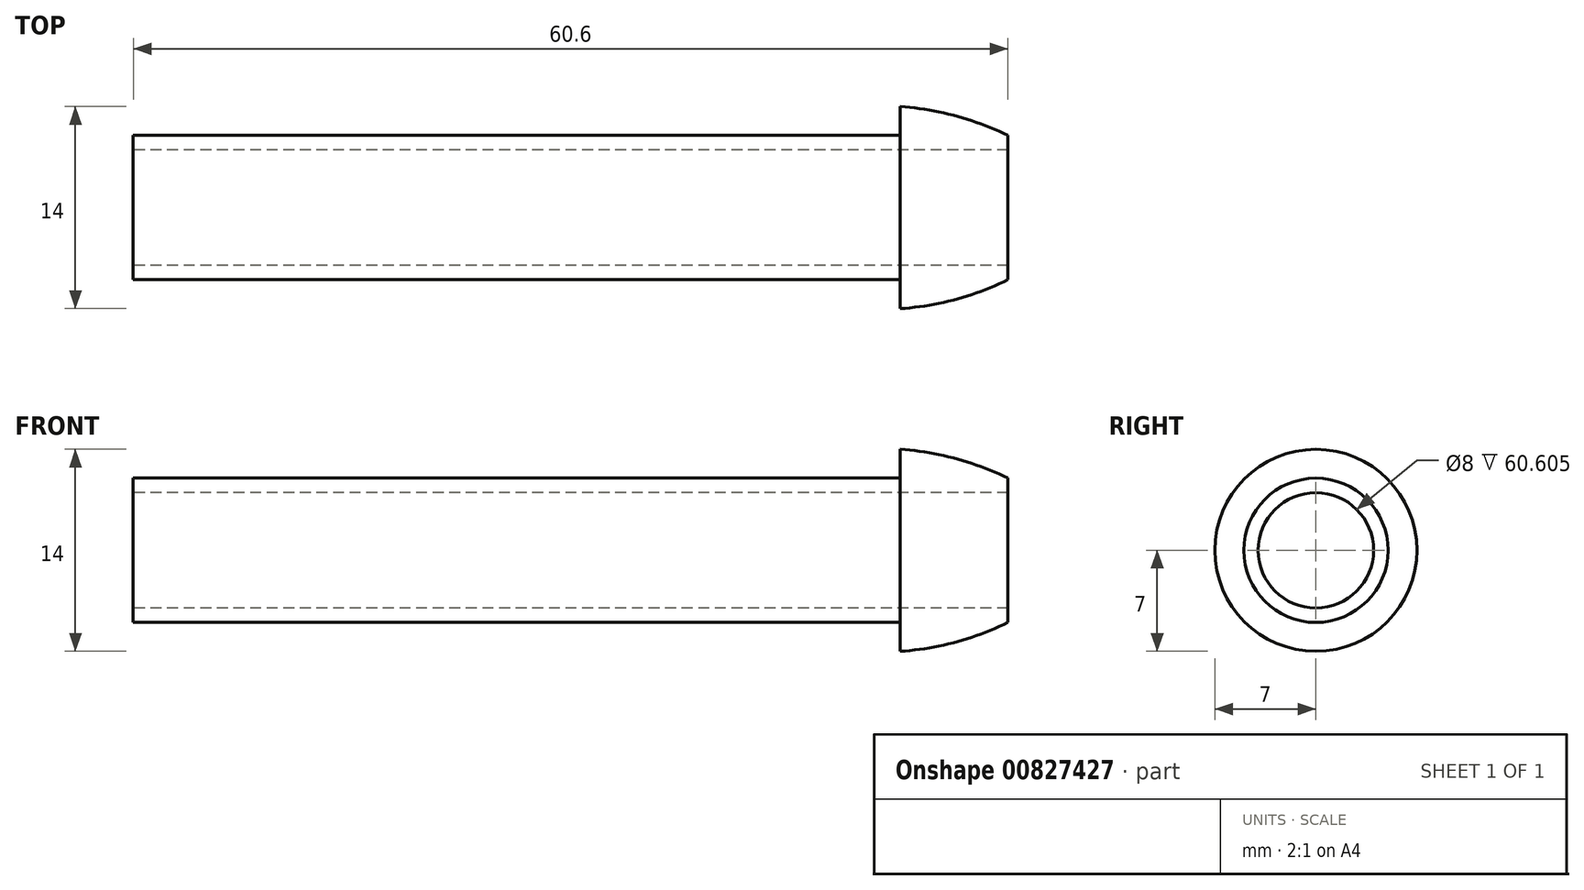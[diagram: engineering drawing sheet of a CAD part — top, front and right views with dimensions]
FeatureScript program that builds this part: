
annotation { "Feature Type Name" : "Feature", "Feature Type Description" : "" }
export const myFeature = defineFeature(function(context is Context, id is Id, definition is map)
    precondition{}
    {
        {
            var Q0;
            Q0=qCreatedBy(makeId("Front.planeOp"),FACE);
            var sketch = newSketch(context, id + "F0", { "sketchPlane" : qUnion([Q0])});
            skLineSegment(sketch, "E0", {"start": v(-39.72, 0) * mm, "end": v(40.92, 0) * mm, "construction": true});
            skLineSegment(sketch, "E1", {"start": v(-60.6, 4) * mm, "end": v(0, 4) * mm});
            skLineSegment(sketch, "E2", {"start": v(0, 4) * mm, "end": v(0, 5) * mm});
            skLineSegment(sketch, "E3", {"start": v(-60.6, 4) * mm, "end": v(-60.6, 5) * mm});
            skLineSegment(sketch, "E4", {"start": v(-60.6, 5) * mm, "end": v(-7.46, 5) * mm});
            skLineSegment(sketch, "E5", {"start": v(-7.46, 5) * mm, "end": v(-7.46, 7) * mm});
            skArc(sketch, "E6", {"start": v(0, 5) * mm, "mid": v(-3.63, 6.36) * mm, "end": v(-7.46, 7) * mm});
            skLineSegment(sketch, "E7", {"start": v(-7.46, 7) * mm, "end": v(0, 5) * mm, "construction": true});
            skSolve(sketch);
        }
        {
            var Q0;
            Q0=makeQuery(id+"F0.imprint","IMPRINT",FACE,{"disambiguationData":[TD([[makeQuery(id+"F0.imprint","IMPRINT",EDGE,{"derivedFrom":sQuery(id+"F0.wireOp",EDGE,"E1")}),1.0]])]});
            var Q1;
            Q1=sQuery(id+"F0.wireOp",EDGE,"E0");
            revolve(context, id + "F1", {"surfaceOperationType" : NewSurfaceOperationType.NEW, "entities" : qUnion([Q0]), "axis" : qUnion([Q1]), "revolveType" : RevolveType.FULL});
        }
    });
